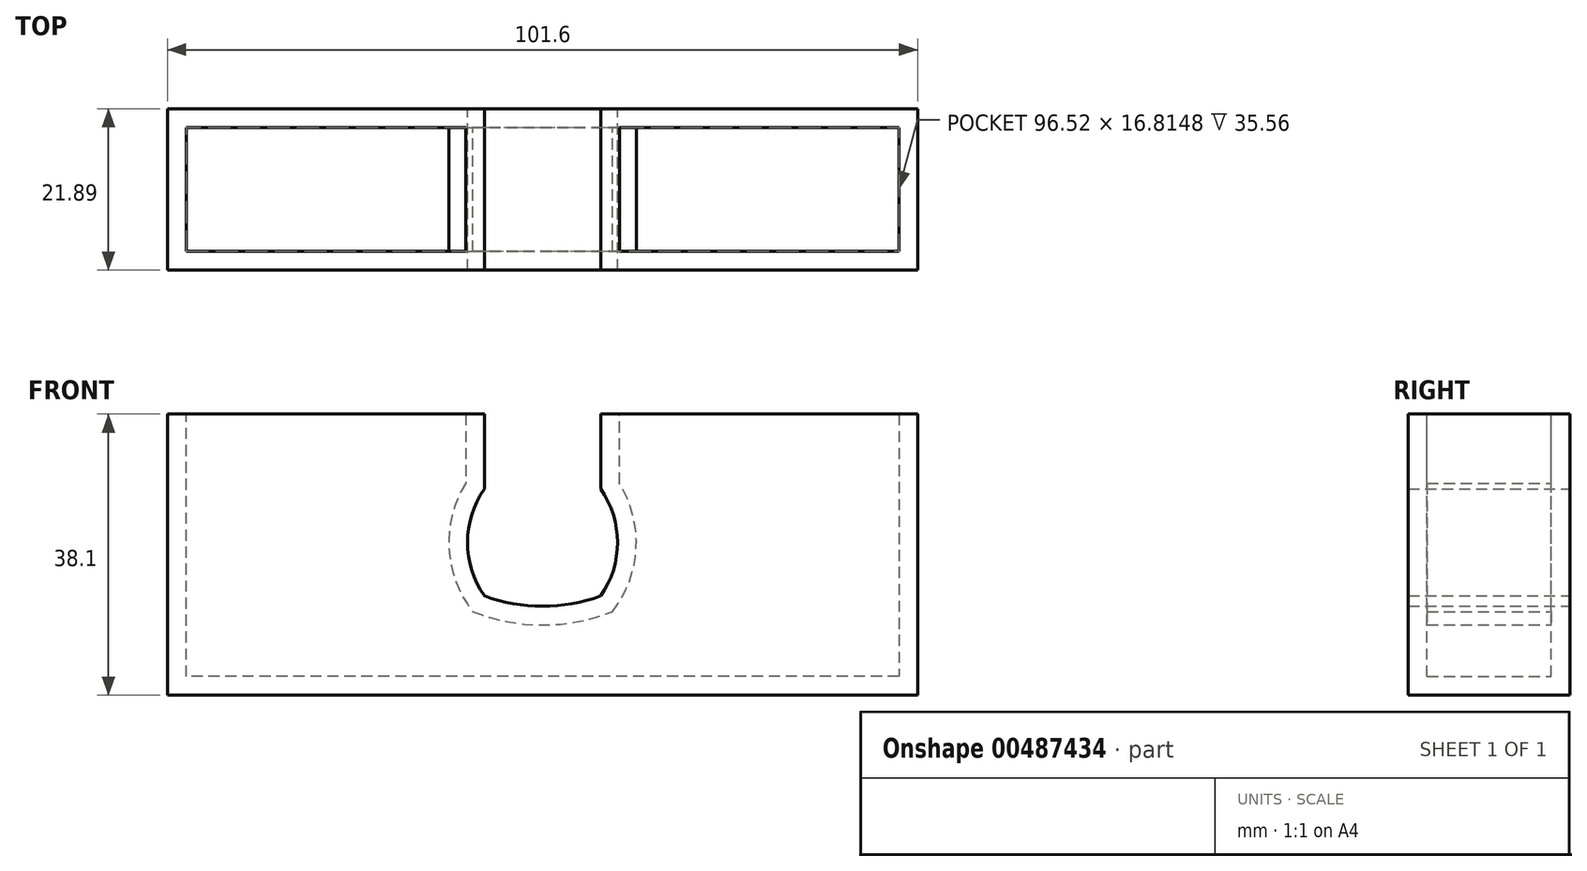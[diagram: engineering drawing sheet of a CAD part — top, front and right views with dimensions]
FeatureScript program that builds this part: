
annotation { "Feature Type Name" : "Feature", "Feature Type Description" : "" }
export const myFeature = defineFeature(function(context is Context, id is Id, definition is map)
    precondition{}
    {
        {
            var Q0;
            Q0=qCreatedBy(makeId("Front.planeOp"),FACE);
            var sketch = newSketch(context, id + "F0", { "sketchPlane" : qUnion([Q0])});
            skLineSegment(sketch, "E0", {"start": v(0, 0) * mm, "end": v(50.8, 0) * mm});
            skLineSegment(sketch, "E1", {"start": v(0, 0) * mm, "end": v(-50.8, 0) * mm});
            skLineSegment(sketch, "E2", {"start": v(-50.8, 0) * mm, "end": v(-50.8, 38.1) * mm});
            skLineSegment(sketch, "E3", {"start": v(-50.8, 38.1) * mm, "end": v(50.8, 38.1) * mm});
            skLineSegment(sketch, "E4", {"start": v(50.8, 38.1) * mm, "end": v(50.8, 0) * mm});
            skSolve(sketch);
        }
        {
            var Q0;
            Q0=makeQuery(id+"F0.imprint","IMPRINT",FACE,{"disambiguationData":[TD([[makeQuery(id+"F0.imprint","IMPRINT",EDGE,{"derivedFrom":sQuery(id+"F0.wireOp",EDGE,"E0")}),1.0]])]});
            extrude(context, id + "F1", {"entities" : qUnion([Q0]), "depth" : 21.9 * mm});
        }
        {
            var Q0;
            Q0=qCreatedBy(makeId("Front.planeOp"),FACE);
            var sketch = newSketch(context, id + "F2", { "sketchPlane" : qUnion([Q0])});
            skLineSegment(sketch, "E5", {"start": v(-7.87, 10.16) * mm, "end": v(-7.87, 0) * mm});
            skArc(sketch, "E6", {"start": v(7.87, 10.16) * mm, "mid": v(10.16, 17.4) * mm, "end": v(7.87, 24.64) * mm});
            skArc(sketch, "E7", {"start": v(-7.87, 24.64) * mm, "mid": v(-10.16, 17.4) * mm, "end": v(-7.87, 10.16) * mm});
            skArc(sketch, "E8", {"start": v(7.87, 24.64) * mm, "mid": v(0, 26.04) * mm, "end": v(-7.87, 24.64) * mm});
            skLineSegment(sketch, "E9", {"start": v(7.87, 0) * mm, "end": v(7.87, 10.16) * mm});
            skLineSegment(sketch, "E10", {"start": v(7.87, 0) * mm, "end": v(-7.87, 0) * mm});
            skSolve(sketch);
        }
        {
            var Q0;
            Q0=makeQuery(id+"F2.imprint","IMPRINT",FACE,{"disambiguationData":[TD([[makeQuery(id+"F2.imprint","IMPRINT",EDGE,{"derivedFrom":sQuery(id+"F2.wireOp",EDGE,"E5")}),1.0]])]});
            extrude(context, id + "F3", {"entities" : qUnion([Q0]), "operationType" : NewBodyOperationType.REMOVE, "depth" : 25.4 * mm});
        }
        {
            var Q0;
            {var subQ0=sQuery(id+"F0.wireOp",EDGE,"E4");var subQ3=sQuery(id+"F0.wireOp",EDGE,"E1");var subQ4=sQuery(id+"F0.wireOp",EDGE,"E0");Q0=makeQuery(id+"F3.boolean.opBoolean","SPLIT",FACE,{"disambiguationData":[TD([makeQuery(id+"F1.opExtrude","SWEPT_FACE",FACE,{"disambiguationData":[OSD([subQ0])]})])],"derivedFrom":makeQuery(id+"F1.opExtrude","SWEPT_FACE",FACE,{"disambiguationData":[OSD([subQ4,subQ3])]})});}
            var Q1;
            {var subQ2=sQuery(id+"F0.wireOp",EDGE,"E2");var subQ3=sQuery(id+"F0.wireOp",EDGE,"E1");var subQ4=sQuery(id+"F0.wireOp",EDGE,"E0");Q1=makeQuery(id+"F3.boolean.opBoolean","SPLIT",FACE,{"disambiguationData":[TD([makeQuery(id+"F1.opExtrude","SWEPT_FACE",FACE,{"disambiguationData":[OSD([subQ2])]})])],"derivedFrom":makeQuery(id+"F1.opExtrude","SWEPT_FACE",FACE,{"disambiguationData":[OSD([subQ4,subQ3])]})});}
            shell(context, id + "F4", {"entities" : qUnion([Q0, Q1]), "thickness" : 2.54 * mm});
        }
        {
            var Q0;
            Q0=makeQuery(id+"F1.opExtrude","SWEPT_BODY",BODY,{"disambiguationData":[OSD([sQuery(id+"F0.wireOp",EDGE,"E0"),sQuery(id+"F0.wireOp",EDGE,"E1"),sQuery(id+"F0.wireOp",EDGE,"E2"),sQuery(id+"F0.wireOp",EDGE,"E3"),sQuery(id+"F0.wireOp",EDGE,"E4")])]});
            var Q1;
            Q1=makeQuery(id+"F1.opExtrude","SWEPT_EDGE",EDGE,{"disambiguationData":[OSD([sQuery(id+"F0.wireOp",EDGE,"E0"),sQuery(id+"F0.wireOp",EDGE,"E4")])]});
            transform(context, id + "F5", {"entities" : qUnion([Q0]), "transformType" : TransformType.ROTATION, "transformAxis" : qUnion([Q1]), "angle" : 180 * degree, "makeCopy" : false});
        }
    });
